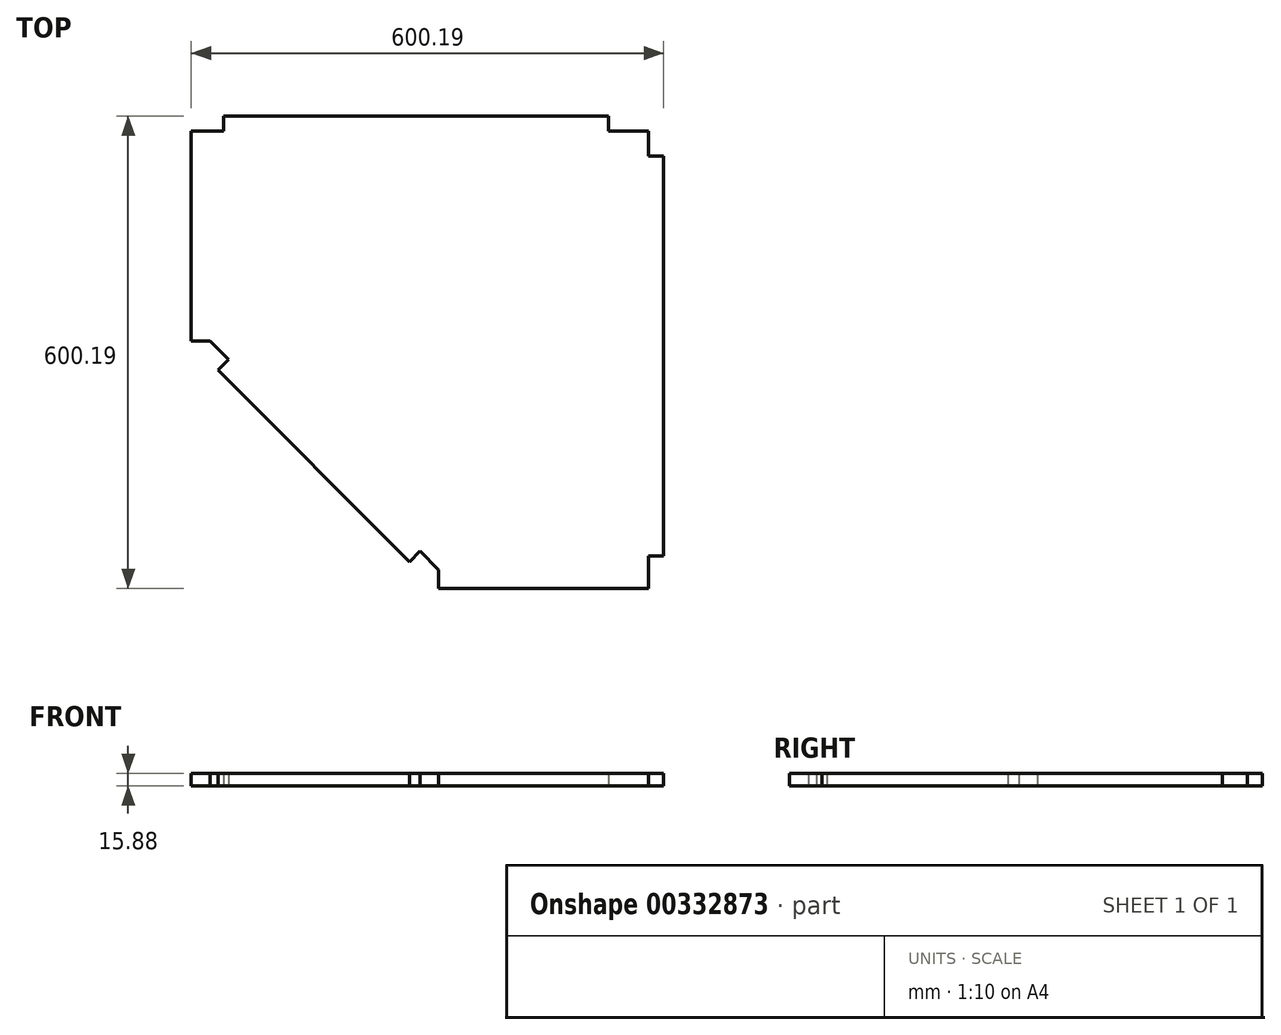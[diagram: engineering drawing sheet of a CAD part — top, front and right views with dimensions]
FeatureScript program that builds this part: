
annotation { "Feature Type Name" : "Feature", "Feature Type Description" : "" }
export const myFeature = defineFeature(function(context is Context, id is Id, definition is map)
    precondition{}
    {
        {
            var Q0;
            Q0=qCreatedBy(makeId("Top.planeOp"),FACE);
            var sketch = newSketch(context, id + "F0", { "sketchPlane" : qUnion([Q0])});
            skPoint(sketch, "E0.middle", {"position": v(0, 0) * mm});
            skPoint(sketch, "E1.orphan", {"position": v(-495.3, -425.45) * mm});
            skLineSegment(sketch, "E2", {"start": v(172.54, -140.9) * mm, "end": v(-71.05, 102.69) * mm});
            skPoint(sketch, "E3.orphan", {"position": v(-495.3, 425.45) * mm});
            skPoint(sketch, "E4.orphan", {"position": v(495.3, -425.45) * mm});
            skLineSegment(sketch, "E5.top", {"start": v(476.25, 406.4) * mm, "end": v(425.45, 406.4) * mm});
            skLineSegment(sketch, "E5.right", {"start": v(425.45, 425.45) * mm, "end": v(425.45, 406.4) * mm});
            skLineSegment(sketch, "E6.bottom", {"start": v(476.25, 374.65) * mm, "end": v(495.3, 374.65) * mm});
            skLineSegment(sketch, "E6.left", {"start": v(476.25, 374.65) * mm, "end": v(476.25, 406.4) * mm});
            skPoint(sketch, "E7.orphan", {"position": v(495.3, 425.45) * mm});
            skLineSegment(sketch, "E8.top", {"start": v(-104.89, 139.7) * mm, "end": v(-81.12, 139.7) * mm});
            skLineSegment(sketch, "E9.right", {"start": v(209.55, -174.74) * mm, "end": v(209.55, -150.97) * mm});
            skLineSegment(sketch, "E10", {"start": v(-81.12, 139.7) * mm, "end": v(-57.58, 116.16) * mm});
            skLineSegment(sketch, "E11", {"start": v(172.54, -140.9) * mm, "end": v(186, -127.43) * mm});
            skPoint(sketch, "E12.orphan", {"position": v(190.5, -158.86) * mm});
            skLineSegment(sketch, "E13", {"start": v(-71.05, 102.69) * mm, "end": v(-57.58, 116.16) * mm});
            skPoint(sketch, "E14.orphan", {"position": v(-89.01, 120.65) * mm});
            skLineSegment(sketch, "E15.trimOffspring", {"start": v(186, -127.43) * mm, "end": v(209.55, -150.97) * mm});
            skLineSegment(sketch, "E16.bottom", {"start": v(-104.89, 406.4) * mm, "end": v(-63.61, 406.4) * mm});
            skLineSegment(sketch, "E16.right", {"start": v(-63.61, 406.4) * mm, "end": v(-63.61, 425.45) * mm});
            skLineSegment(sketch, "E17.top", {"start": v(476.25, -133.46) * mm, "end": v(495.3, -133.46) * mm});
            skLineSegment(sketch, "E17.left", {"start": v(476.25, -174.74) * mm, "end": v(476.25, -133.46) * mm});
            skLineSegment(sketch, "E18.trimOffspring", {"start": v(-63.61, 425.45) * mm, "end": v(425.45, 425.45) * mm});
            skLineSegment(sketch, "E19.trimOffspring", {"start": v(495.3, -133.46) * mm, "end": v(495.3, 374.65) * mm});
            skPoint(sketch, "E20.orphan", {"position": v(-1790.7, 425.45) * mm});
            skPoint(sketch, "E21.orphan", {"position": v(-1358.9, 437.81) * mm});
            skPoint(sketch, "E22.top.start.orphan", {"position": v(476.25, -374.76) * mm});
            skLineSegment(sketch, "E23", {"start": v(209.55, -174.74) * mm, "end": v(476.25, -174.74) * mm});
            skPoint(sketch, "E24.orphan", {"position": v(476.25, -184.26) * mm});
            skPoint(sketch, "E25.orphan", {"position": v(209.55, -184.26) * mm});
            skLineSegment(sketch, "E26", {"start": v(-104.89, 406.4) * mm, "end": v(-104.89, 139.7) * mm});
            skPoint(sketch, "E16.left.start.orphan", {"position": v(-114.41, 406.4) * mm});
            skPoint(sketch, "E27.orphan", {"position": v(-114.41, 139.7) * mm});
            skPoint(sketch, "E28.right.start.orphan", {"position": v(-444.5, 120.65) * mm});
            skPoint(sketch, "E28.top.end.orphan", {"position": v(-444.5, 139.7) * mm});
            skPoint(sketch, "E29.bottom.start.orphan", {"position": v(-495.3, 120.65) * mm});
            skPoint(sketch, "E30.top.end.orphan", {"position": v(-444.5, 406.4) * mm});
            skPoint(sketch, "E31.left.start.orphan", {"position": v(-1358.9, 139.7) * mm});
            skPoint(sketch, "E32.bottom.start.orphan", {"position": v(-1308.1, 406.4) * mm});
            skPoint(sketch, "E33.bottom.end.orphan", {"position": v(-1739.9, 139.7) * mm});
            skPoint(sketch, "E34.right.end.orphan", {"position": v(-1739.9, 406.4) * mm});
            skSolve(sketch);
        }
        {
            var Q0;
            Q0=qSketchRegion(id+"F0",true);
            extrude(context, id + "F1", {"entities" : qUnion([Q0]), "depth" : 15.88 * mm});
        }
    });
